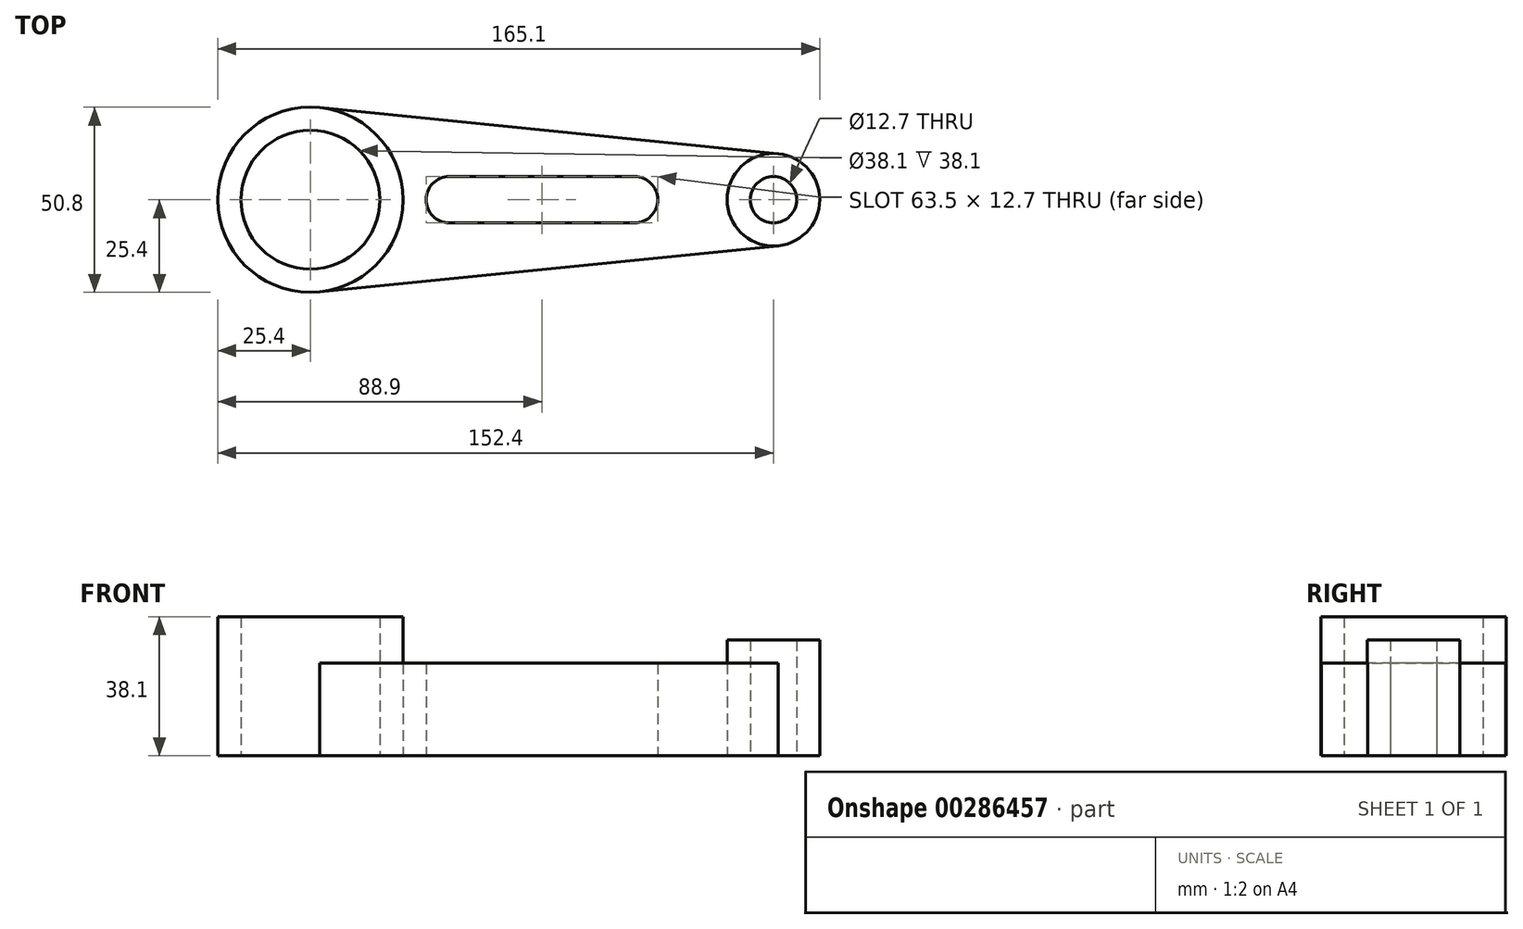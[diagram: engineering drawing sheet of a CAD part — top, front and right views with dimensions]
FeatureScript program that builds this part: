
annotation { "Feature Type Name" : "Feature", "Feature Type Description" : "" }
export const myFeature = defineFeature(function(context is Context, id is Id, definition is map)
    precondition{}
    {
        {
            var Q0;
            Q0=qCreatedBy(makeId("Top.planeOp"),FACE);
            var sketch = newSketch(context, id + "F0", { "sketchPlane" : qUnion([Q0])});
            skCircle(sketch, "E0", {"center": v(-38.1, 0) * mm, "radius": 19.05 * mm});
            skCircle(sketch, "E1", {"center": v(-38.1, 0) * mm, "radius": 25.4 * mm});
            skArc(sketch, "E2", {"start": v(0, 6.35) * mm, "mid": v(-6.35, 0) * mm, "end": v(0, -6.35) * mm});
            skArc(sketch, "E3", {"start": v(50.8, -6.35) * mm, "mid": v(57.15, 0) * mm, "end": v(50.8, 6.35) * mm});
            skCircle(sketch, "E4", {"center": v(88.9, 0) * mm, "radius": 6.35 * mm});
            skCircle(sketch, "E5", {"center": v(88.9, 0) * mm, "radius": 12.7 * mm});
            skLineSegment(sketch, "E6", {"start": v(-35.56, 25.27) * mm, "end": v(90.17, 12.64) * mm});
            skLineSegment(sketch, "E7", {"start": v(-35.56, -25.27) * mm, "end": v(90.17, -12.64) * mm});
            skLineSegment(sketch, "E8", {"start": v(0, 6.35) * mm, "end": v(50.8, 6.35) * mm});
            skLineSegment(sketch, "E9", {"start": v(0, -6.35) * mm, "end": v(50.8, -6.35) * mm});
            skSolve(sketch);
        }
        {
            var Q0;
            Q0=makeQuery(id+"F0.imprint","IMPRINT",FACE,{"disambiguationData":[TD([[makeQuery(id+"F0.imprint","IMPRINT",EDGE,{"derivedFrom":sQuery(id+"F0.wireOp",EDGE,"E0")}),-1.0]])]});
            extrude(context, id + "F1", {"entities" : qUnion([Q0]), "depth" : 38.1 * mm});
        }
        {
            var Q0;
            Q0=makeQuery(id+"F0.imprint","IMPRINT",FACE,{"disambiguationData":[TD([[makeQuery(id+"F0.imprint","IMPRINT",EDGE,{"derivedFrom":sQuery(id+"F0.wireOp",EDGE,"E4")}),-1.0]])]});
            extrude(context, id + "F2", {"entities" : qUnion([Q0]), "depth" : 31.75 * mm});
        }
        {
            var Q0;
            Q0=makeQuery(id+"F0.imprint","IMPRINT",FACE,{"disambiguationData":[TD([[makeQuery(id+"F0.imprint","IMPRINT",EDGE,{"derivedFrom":sQuery(id+"F0.wireOp",EDGE,"E2")}),-1.0]])]});
            extrude(context, id + "F3", {"entities" : qUnion([Q0]), "depth" : 25.4 * mm});
        }
    });
